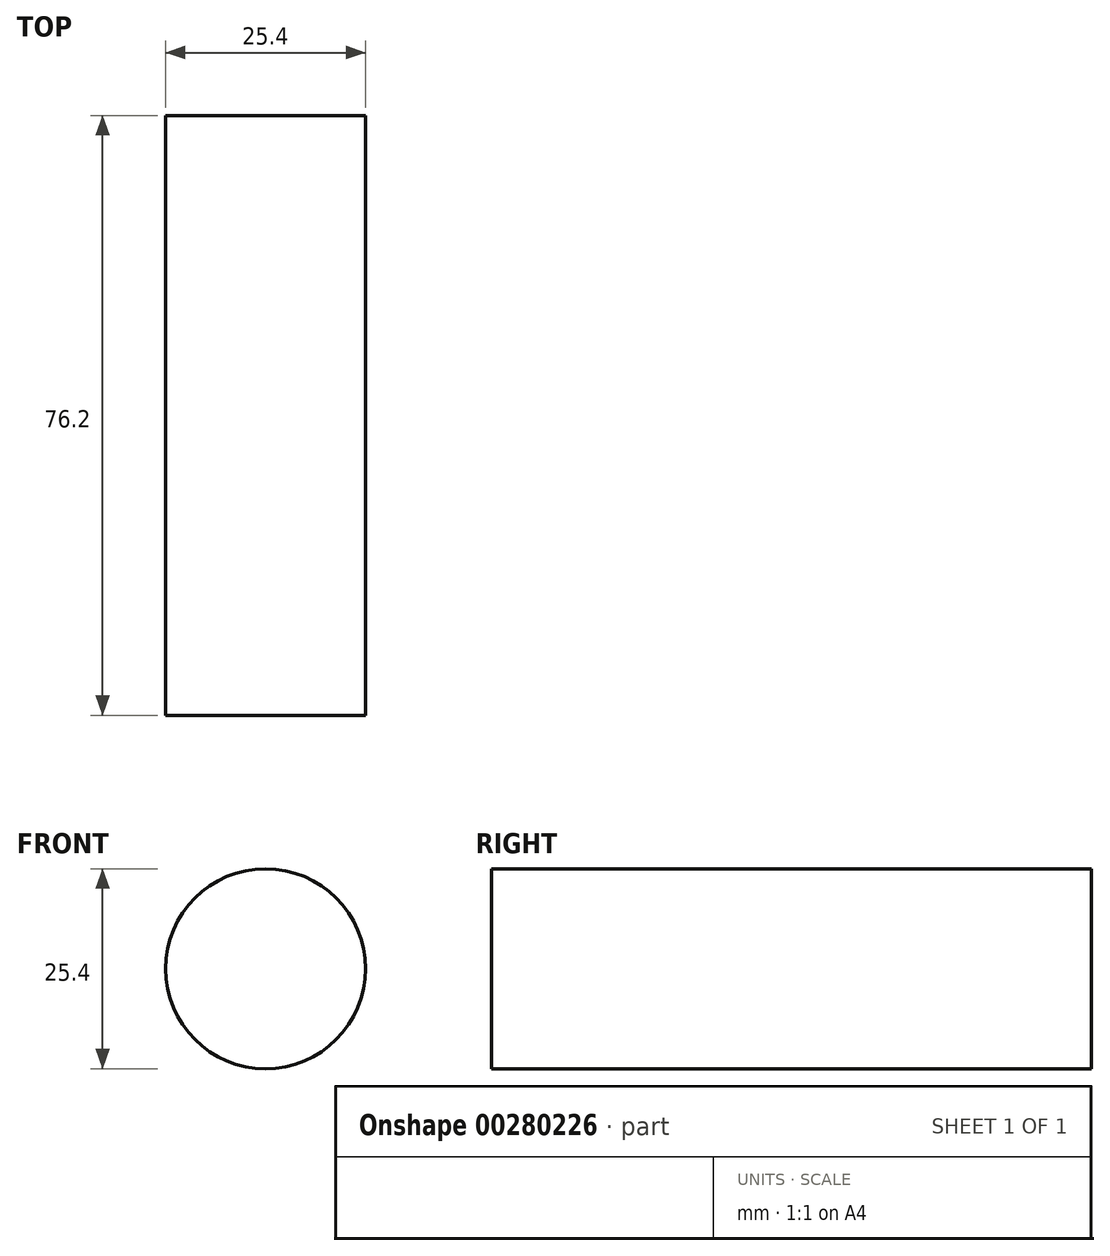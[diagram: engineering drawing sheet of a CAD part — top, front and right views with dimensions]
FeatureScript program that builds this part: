
annotation { "Feature Type Name" : "Feature", "Feature Type Description" : "" }
export const myFeature = defineFeature(function(context is Context, id is Id, definition is map)
    precondition{}
    {
        {
            var Q0;
            Q0=qCreatedBy(makeId("Front.planeOp"),FACE);
            var sketch = newSketch(context, id + "F0", { "sketchPlane" : qUnion([Q0])});
            skCircle(sketch, "E0", {"center": v(-54.61, 33.04) * mm, "radius": 12.7 * mm});
            skSolve(sketch);
        }
        {
            var Q0;
            Q0 = qSketchRegion(id + "F0", true);
            extrude(context, id + "F1", {"entities" : qUnion([Q0]), "depth" : 76.2 * mm});
        }
    });
